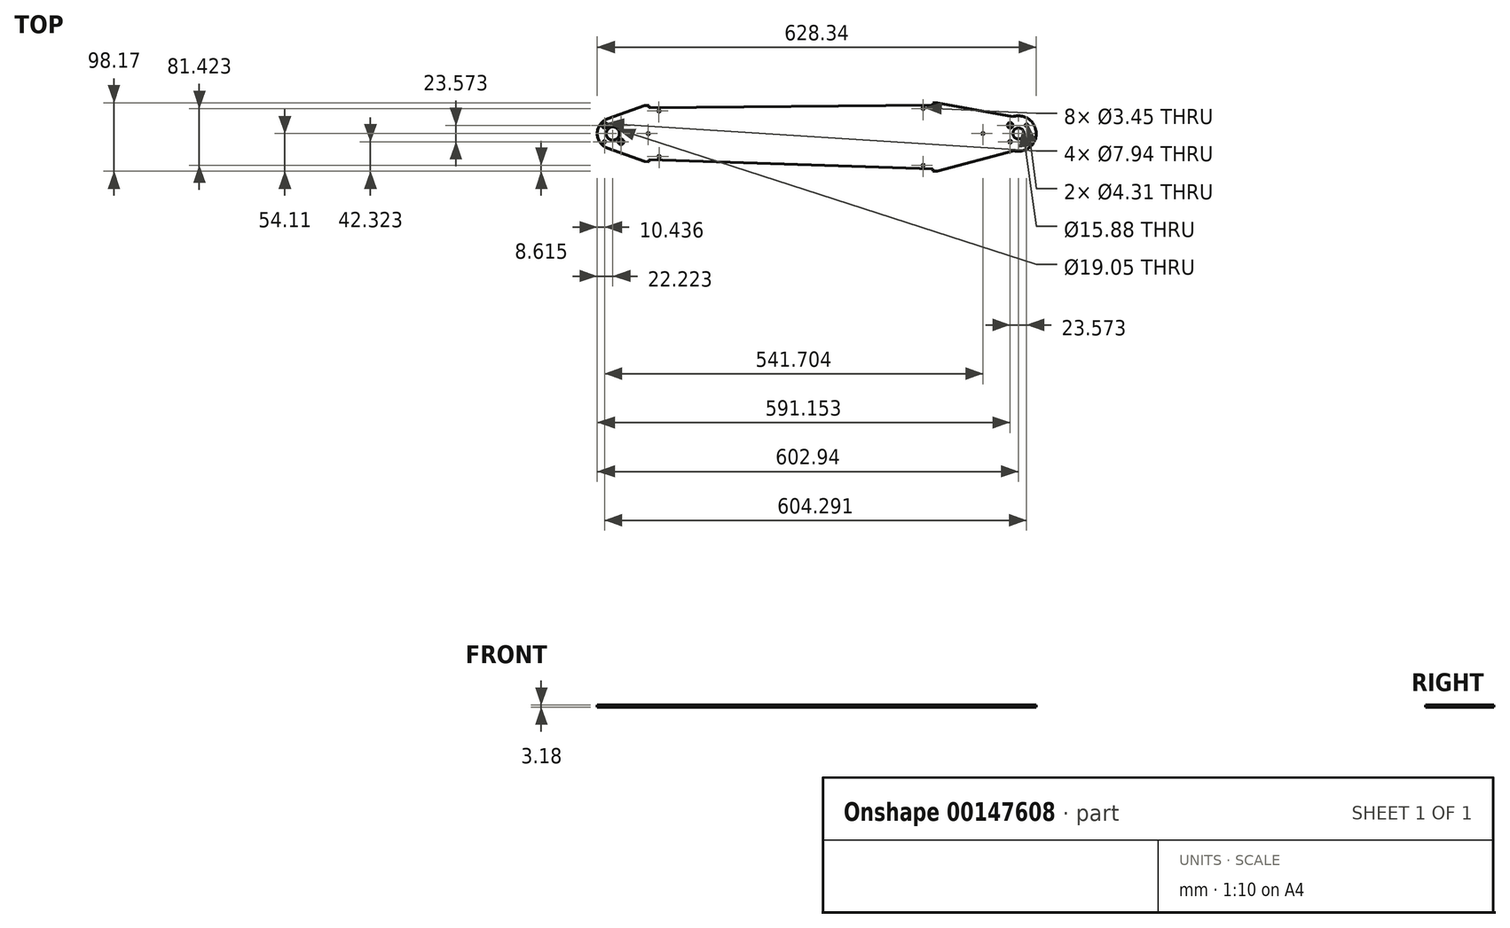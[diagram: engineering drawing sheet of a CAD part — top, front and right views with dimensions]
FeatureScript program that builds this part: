
annotation { "Feature Type Name" : "Feature", "Feature Type Description" : "" }
export const myFeature = defineFeature(function(context is Context, id is Id, definition is map)
    precondition{}
    {
        {
            var Q0;
            Q0=qCreatedBy(makeId("Top.planeOp"),FACE);
            var sketch = newSketch(context, id + "F0", { "sketchPlane" : qUnion([Q0])});
            skPoint(sketch, "E0.rect.middle", {"position": v(0, 0) * mm});
            skCircle(sketch, "E1", {"center": v(0, 0) * mm, "radius": 7.94 * mm});
            skLineSegment(sketch, "E2.bottom", {"start": v(11.79, 11.79) * mm, "end": v(-11.79, 11.79) * mm, "construction": true});
            skLineSegment(sketch, "E2.left", {"start": v(11.79, 11.79) * mm, "end": v(11.79, -11.79) * mm, "construction": true});
            skLineSegment(sketch, "E2.right", {"start": v(-11.79, 11.79) * mm, "end": v(-11.79, -11.79) * mm, "construction": true});
            skCircle(sketch, "E3", {"center": v(-11.79, 11.79) * mm, "radius": 3.97 * mm});
            skCircle(sketch, "E4", {"center": v(11.79, 11.79) * mm, "radius": 2.15 * mm});
            skCircle(sketch, "E5", {"center": v(11.79, -11.79) * mm, "radius": 3.97 * mm});
            skCircle(sketch, "E6", {"center": v(-11.79, -11.79) * mm, "radius": 2.15 * mm});
            skArc(sketch, "E7", {"start": v(-588.32, 20.88) * mm, "mid": v(-602.94, 0) * mm, "end": v(-588.32, -20.88) * mm});
            skLineSegment(sketch, "E8.bottom", {"start": v(-592.5, 11.79) * mm, "end": v(-568.93, 11.79) * mm, "construction": true});
            skLineSegment(sketch, "E8.top", {"start": v(-592.5, -11.79) * mm, "end": v(-568.93, -11.79) * mm, "construction": true});
            skLineSegment(sketch, "E8.left", {"start": v(-592.5, 11.79) * mm, "end": v(-592.5, -11.79) * mm, "construction": true});
            skLineSegment(sketch, "E8.right", {"start": v(-568.93, 11.79) * mm, "end": v(-568.93, -11.79) * mm, "construction": true});
            skCircle(sketch, "E9", {"center": v(-568.93, 11.79) * mm, "radius": 1.73 * mm});
            skCircle(sketch, "E10", {"center": v(-580.72, 0) * mm, "radius": 9.53 * mm});
            skCircle(sketch, "E11", {"center": v(-592.5, 11.79) * mm, "radius": 3.97 * mm});
            skCircle(sketch, "E12", {"center": v(-592.5, -11.79) * mm, "radius": 1.73 * mm});
            skCircle(sketch, "E13", {"center": v(-568.93, -11.79) * mm, "radius": 3.97 * mm});
            skLineSegment(sketch, "E14", {"start": v(0, 0) * mm, "end": v(-580.72, 0) * mm, "construction": true});
            skLineSegment(sketch, "E15", {"start": v(-588.32, -20.88) * mm, "end": v(-535.36, -40.16) * mm});
            skLineSegment(sketch, "E16", {"start": v(-588.32, 20.88) * mm, "end": v(-535.36, 40.16) * mm});
            skLineSegment(sketch, "E17", {"start": v(-528.9, -37.2) * mm, "end": v(-122.33, -50.73) * mm});
            skLineSegment(sketch, "E18", {"start": v(-528.98, 37.04) * mm, "end": v(-122.2, 40.82) * mm});
            skLineSegment(sketch, "E19", {"start": v(-529, 40.22) * mm, "end": v(-528.98, 37.04) * mm});
            skLineSegment(sketch, "E20", {"start": v(-529, 40.22) * mm, "end": v(-535.36, 40.16) * mm});
            skLineSegment(sketch, "E21", {"start": v(-528.9, -37.2) * mm, "end": v(-529.01, -40.37) * mm});
            skLineSegment(sketch, "E22", {"start": v(-529.01, -40.37) * mm, "end": v(-535.36, -40.16) * mm});
            skLineSegment(sketch, "E23", {"start": v(-122.33, -50.73) * mm, "end": v(-122.43, -53.9) * mm});
            skLineSegment(sketch, "E24", {"start": v(-122.2, 40.82) * mm, "end": v(-122.22, 44) * mm});
            skLineSegment(sketch, "E25", {"start": v(-528.98, 37.04) * mm, "end": v(-528.93, 32.28) * mm, "construction": true});
            skLineSegment(sketch, "E26", {"start": v(-528.93, 32.28) * mm, "end": v(-514.65, 32.42) * mm, "construction": true});
            skLineSegment(sketch, "E27", {"start": v(-528.9, -37.2) * mm, "end": v(-528.75, -32.44) * mm, "construction": true});
            skLineSegment(sketch, "E28", {"start": v(-122.33, -50.73) * mm, "end": v(-122.17, -45.97) * mm, "construction": true});
            skLineSegment(sketch, "E29", {"start": v(-122.17, -45.97) * mm, "end": v(-136.45, -45.5) * mm, "construction": true});
            skLineSegment(sketch, "E30", {"start": v(-122.2, 40.82) * mm, "end": v(-122.15, 36.06) * mm, "construction": true});
            skLineSegment(sketch, "E31", {"start": v(-122.15, 36.06) * mm, "end": v(-136.43, 35.93) * mm, "construction": true});
            skCircle(sketch, "E32", {"center": v(-514.65, 32.42) * mm, "radius": 1.73 * mm});
            skCircle(sketch, "E33", {"center": v(-136.43, 35.93) * mm, "radius": 1.73 * mm});
            skCircle(sketch, "E34", {"center": v(-136.45, -45.5) * mm, "radius": 1.73 * mm});
            skCircle(sketch, "E35", {"center": v(-514.47, -32.91) * mm, "radius": 1.73 * mm});
            skLineSegment(sketch, "E36", {"start": v(-11.79, -11.79) * mm, "end": v(11.79, -11.79) * mm, "construction": true});
            skLineSegment(sketch, "E37", {"start": v(-568.93, 11.79) * mm, "end": v(-529.92, 11.79) * mm, "construction": true});
            skLineSegment(sketch, "E38", {"start": v(-529.92, 11.79) * mm, "end": v(-529.92, 0) * mm, "construction": true});
            skLineSegment(sketch, "E39", {"start": v(-11.79, 11.79) * mm, "end": v(-50.8, 11.79) * mm, "construction": true});
            skLineSegment(sketch, "E40", {"start": v(-50.8, 11.79) * mm, "end": v(-50.8, 0) * mm, "construction": true});
            skCircle(sketch, "E41", {"center": v(-529.92, 0) * mm, "radius": 1.73 * mm});
            skCircle(sketch, "E42", {"center": v(-50.8, 0) * mm, "radius": 1.73 * mm});
            skLineSegment(sketch, "E43", {"start": v(-588.32, -20.88) * mm, "end": v(-561.84, -20.88) * mm, "construction": true});
            skLineSegment(sketch, "E44", {"start": v(-561.84, -20.88) * mm, "end": v(-561.84, -30.52) * mm, "construction": true});
            skLineSegment(sketch, "E45", {"start": v(-588.32, -20.88) * mm, "end": v(-588.32, 20.88) * mm, "construction": true});
            skLineSegment(sketch, "E46", {"start": v(-592.5, 0) * mm, "end": v(-588.32, 0) * mm, "construction": true});
            skLineSegment(sketch, "E47", {"start": v(-528.75, -32.44) * mm, "end": v(-514.47, -32.91) * mm, "construction": true});
            skPoint(sketch, "E48.endSnap0", {"position": v(0, 11.79) * mm});
            skCircle(sketch, "E49", {"center": v(-580.72, 0) * mm, "radius": 24.52 * mm, "construction": true});
            skLineSegment(sketch, "E50", {"start": v(-122.22, 44) * mm, "end": v(-115.87, 44.06) * mm});
            skLineSegment(sketch, "E51", {"start": v(-122.43, -53.9) * mm, "end": v(-116.09, -54.11) * mm});
            skLineSegment(sketch, "E52", {"start": v(-116.09, -54.11) * mm, "end": v(-6.13, -24.65) * mm});
            skLineSegment(sketch, "E53", {"start": v(-115.87, 44.06) * mm, "end": v(-8.04, 24.1) * mm});
            skLineSegment(sketch, "E54", {"start": v(-8.04, 24.1) * mm, "end": v(4.05, 21.85) * mm, "construction": true});
            skLineSegment(sketch, "E55", {"start": v(-6.13, -24.65) * mm, "end": v(5.75, -21.47) * mm, "construction": true});
            skArc(sketch, "E56", {"start": v(5.75, -21.47) * mm, "mid": v(22.2, 0.87) * mm, "end": v(4.05, 21.85) * mm, "construction": true});
            skArc(sketch, "E57", {"start": v(-6.13, -24.65) * mm, "mid": v(25.38, 1) * mm, "end": v(-8.04, 24.1) * mm});
            skSolve(sketch);
        }
        {
            var Q0;
            Q0=qSketchRegion(id+"F0",true);
            extrude(context, id + "F1", {"entities" : qUnion([Q0]), "depth" : 3.17 * mm});
        }
    });
